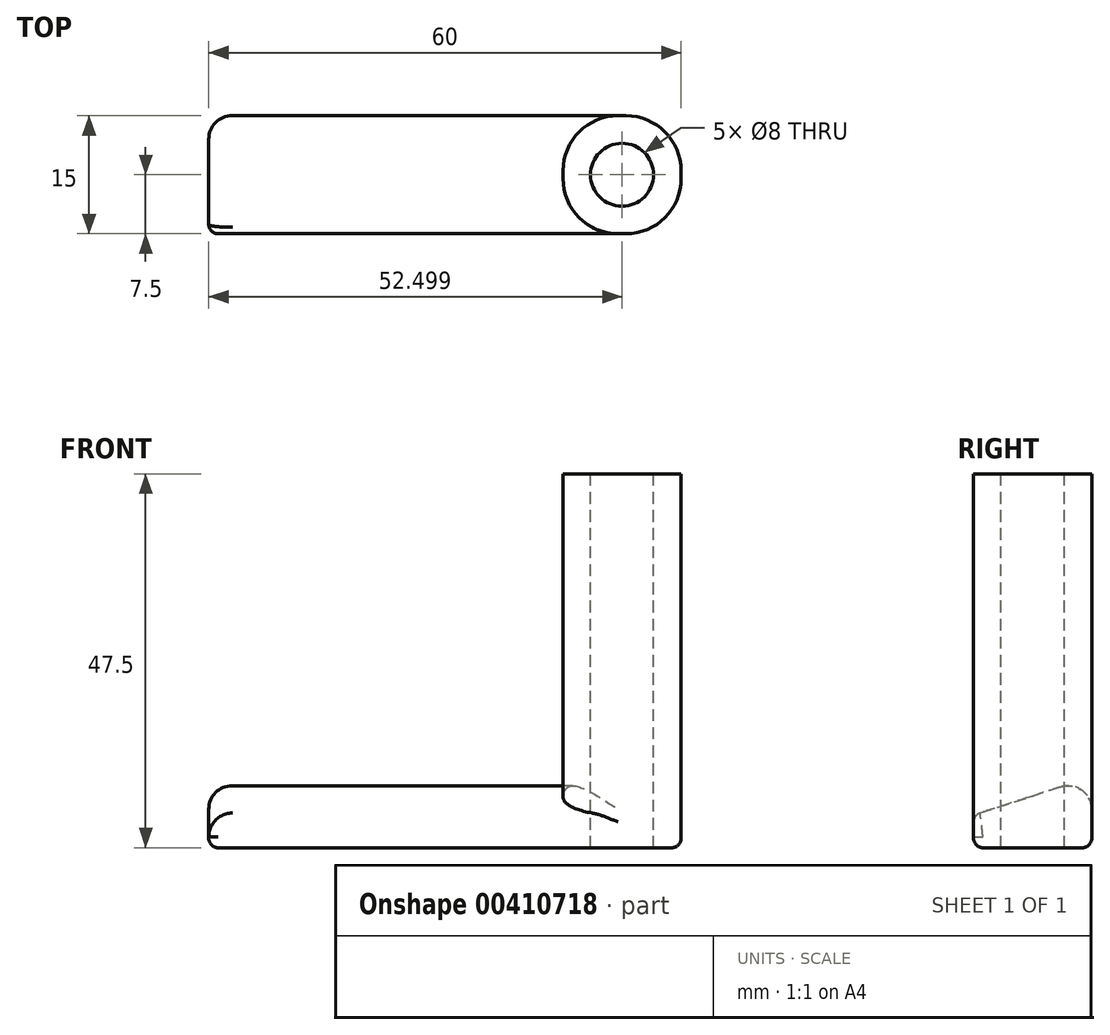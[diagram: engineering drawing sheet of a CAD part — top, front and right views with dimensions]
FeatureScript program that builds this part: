
annotation { "Feature Type Name" : "Feature", "Feature Type Description" : "" }
export const myFeature = defineFeature(function(context is Context, id is Id, definition is map)
    precondition{}
    {
        {
            var Q0;
            Q0=qCreatedBy(makeId("Front.planeOp"),FACE);
            var sketch = newSketch(context, id + "F0", { "sketchPlane" : qUnion([Q0])});
            skLineSegment(sketch, "E0", {"start": v(-36.94, 0) * mm, "end": v(23.06, 0) * mm});
            skLineSegment(sketch, "E1", {"start": v(23.06, 0) * mm, "end": v(23.06, 47.5) * mm});
            skLineSegment(sketch, "E2", {"start": v(23.06, 47.5) * mm, "end": v(8.06, 47.5) * mm});
            skLineSegment(sketch, "E3", {"start": v(-36.94, 9.15) * mm, "end": v(-36.94, 0) * mm});
            skLineSegment(sketch, "E4", {"start": v(8.06, 47.5) * mm, "end": v(8.06, 9.15) * mm});
            skLineSegment(sketch, "E5", {"start": v(8.06, 9.15) * mm, "end": v(-36.94, 9.15) * mm});
            skSolve(sketch);
        }
        {
            var Q0;
            Q0=makeQuery(id+"F0.imprint","IMPRINT",FACE,{"disambiguationData":[TD([[makeQuery(id+"F0.imprint","IMPRINT",EDGE,{"derivedFrom":sQuery(id+"F0.wireOp",EDGE,"E0")}),1.0]])]});
            extrude(context, id + "F1", {"entities" : qUnion([Q0]), "depth" : 15 * mm});
        }
        {
            var Q0;
            Q0=makeQuery(id+"F1.opExtrude","SWEPT_FACE",FACE,{"disambiguationData":[OSD([sQuery(id+"F0.wireOp",EDGE,"E2")])]});
            var sketch = newSketch(context, id + "F2", { "sketchPlane" : qUnion([Q0])});
            skCircle(sketch, "E6", {"center": v(15.56, -7.5) * mm, "radius": 4 * mm});
            skPoint(sketch, "E6.centerSnap0", {"position": v(15.56, 0) * mm});
            skPoint(sketch, "E6.centerSnap1", {"position": v(23.06, -7.5) * mm});
            skSolve(sketch);
        }
        {
            var Q0;
            Q0=makeQuery(id+"F2.imprint","IMPRINT",FACE,{"disambiguationData":[TD([[makeQuery(id+"F2.imprint","IMPRINT",EDGE,{"derivedFrom":sQuery(id+"F2.wireOp",EDGE,"E6")}),1.0]])]});
            extrude(context, id + "F3", {"entities" : qUnion([Q0]), "operationType" : NewBodyOperationType.REMOVE, "oppositeDirection" : true, "depth" : 55.9 * mm});
        }
        {
            var Q0;
            Q0=makeQuery(id+"F1.opExtrude","CAP_EDGE",EDGE,{"disambiguationData":[OSD([sQuery(id+"F0.wireOp",EDGE,"E5")])],"isStart":false});
            chamfer(context, id + "F4", {"entities" : qUnion([Q0]), "chamferType" : ChamferType.OFFSET_ANGLE, "width" : 5 * mm, "oppositeDirection" : false, "angle" : 72 * degree, "tangentPropagation" : true});
        }
        {
            var Q0;
            Q0=makeQuery(id+"F1.opExtrude","CAP_EDGE",EDGE,{"disambiguationData":[OSD([sQuery(id+"F0.wireOp",EDGE,"E4")])],"isStart":false});
            var Q1;
            Q1=makeQuery(id+"F1.opExtrude","CAP_EDGE",EDGE,{"disambiguationData":[OSD([sQuery(id+"F0.wireOp",EDGE,"E4")])],"isStart":true});
            var Q2;
            Q2=makeQuery(id+"F1.opExtrude","CAP_EDGE",EDGE,{"disambiguationData":[OSD([sQuery(id+"F0.wireOp",EDGE,"E1")])],"isStart":true});
            var Q3;
            Q3=makeQuery(id+"F1.opExtrude","CAP_EDGE",EDGE,{"disambiguationData":[OSD([sQuery(id+"F0.wireOp",EDGE,"E1")])],"isStart":false});
            fillet(context, id + "F5", {"entities" : qUnion([Q0, Q1, Q2, Q3]), "radius" : 7 * mm, "tangentPropagation" : true, "allowEdgeOverflow" : false});
        }
        {
            var Q0;
            {var subQ0=sQuery(id+"F0.wireOp",EDGE,"E5");Q0=makeQuery(id+"F4.opChamfer","BLEND_EDGE",EDGE,{"blendedFrom":[makeQuery(id+"F1.opExtrude","CAP_EDGE",EDGE,{"disambiguationData":[OSD([subQ0])],"isStart":false}),makeQuery(id+"F1.opExtrude","CAP_FACE",FACE,{"disambiguationData":[OSD([sQuery(id+"F0.wireOp",EDGE,"E0"),sQuery(id+"F0.wireOp",EDGE,"E1"),sQuery(id+"F0.wireOp",EDGE,"E2"),sQuery(id+"F0.wireOp",EDGE,"E3"),sQuery(id+"F0.wireOp",EDGE,"E4"),subQ0])],"isStart":true})],"blendedInto":[makeQuery(id+"F1.opExtrude","CAP_FACE",FACE,{"disambiguationData":[OSD([sQuery(id+"F0.wireOp",EDGE,"E0"),sQuery(id+"F0.wireOp",EDGE,"E1"),sQuery(id+"F0.wireOp",EDGE,"E2"),sQuery(id+"F0.wireOp",EDGE,"E3"),sQuery(id+"F0.wireOp",EDGE,"E4"),subQ0])],"isStart":true})]});}
            fillet(context, id + "F6", {"entities" : qUnion([Q0]), "radius" : 3 * mm, "tangentPropagation" : true, "allowEdgeOverflow" : false});
        }
        {
            var Q0;
            Q0=makeQuery(id+"F1.opExtrude","CAP_EDGE",EDGE,{"disambiguationData":[OSD([sQuery(id+"F0.wireOp",EDGE,"E3")])],"isStart":true});
            fillet(context, id + "F7", {"entities" : qUnion([Q0]), "radius" : 3 * mm, "tangentPropagation" : true, "allowEdgeOverflow" : false});
        }
        {
            var Q0;
            Q0=makeQuery(id+"F1.opExtrude","CAP_EDGE",EDGE,{"disambiguationData":[OSD([sQuery(id+"F0.wireOp",EDGE,"E0")])],"isStart":true});
            var Q1;
            Q1=makeQuery(id+"F1.opExtrude","CAP_EDGE",EDGE,{"disambiguationData":[OSD([sQuery(id+"F0.wireOp",EDGE,"E0")])],"isStart":false});
            var Q2;
            Q2=makeQuery(id+"F5.opFillet","BLEND_EDGE",EDGE,{"blendedFrom":[makeQuery(id+"F1.opExtrude","CAP_EDGE",EDGE,{"disambiguationData":[OSD([sQuery(id+"F0.wireOp",EDGE,"E1")])],"isStart":true}),makeQuery(id+"F1.opExtrude","SWEPT_FACE",FACE,{"disambiguationData":[OSD([sQuery(id+"F0.wireOp",EDGE,"E0")])]})],"blendedInto":[makeQuery(id+"F1.opExtrude","SWEPT_FACE",FACE,{"disambiguationData":[OSD([sQuery(id+"F0.wireOp",EDGE,"E0")])]})]});
            var Q3;
            Q3=makeQuery(id+"F5.opFillet","BLEND_EDGE",EDGE,{"blendedFrom":[makeQuery(id+"F1.opExtrude","CAP_EDGE",EDGE,{"disambiguationData":[OSD([sQuery(id+"F0.wireOp",EDGE,"E1")])],"isStart":false}),makeQuery(id+"F1.opExtrude","SWEPT_FACE",FACE,{"disambiguationData":[OSD([sQuery(id+"F0.wireOp",EDGE,"E0")])]})],"blendedInto":[makeQuery(id+"F1.opExtrude","SWEPT_FACE",FACE,{"disambiguationData":[OSD([sQuery(id+"F0.wireOp",EDGE,"E0")])]})]});
            var Q4;
            Q4=makeQuery(id+"F1.opExtrude","SWEPT_EDGE",EDGE,{"disambiguationData":[OSD([sQuery(id+"F0.wireOp",EDGE,"E0"),sQuery(id+"F0.wireOp",EDGE,"E1")])]});
            var Q5;
            Q5=makeQuery(id+"F7.opFillet","BLEND_EDGE",EDGE,{"blendedFrom":[makeQuery(id+"F1.opExtrude","CAP_EDGE",EDGE,{"disambiguationData":[OSD([sQuery(id+"F0.wireOp",EDGE,"E3")])],"isStart":true}),makeQuery(id+"F1.opExtrude","SWEPT_FACE",FACE,{"disambiguationData":[OSD([sQuery(id+"F0.wireOp",EDGE,"E0")])]})],"blendedInto":[makeQuery(id+"F1.opExtrude","SWEPT_FACE",FACE,{"disambiguationData":[OSD([sQuery(id+"F0.wireOp",EDGE,"E0")])]})]});
            var Q6;
            Q6=makeQuery(id+"F1.opExtrude","SWEPT_EDGE",EDGE,{"disambiguationData":[OSD([sQuery(id+"F0.wireOp",EDGE,"E0"),sQuery(id+"F0.wireOp",EDGE,"E3")])]});
            var Q7;
            {var subQ0=sQuery(id+"F0.wireOp",EDGE,"E5");Q7=makeQuery(id+"F4.opChamfer","BLEND_EDGE",EDGE,{"blendedFrom":[makeQuery(id+"F1.opExtrude","CAP_EDGE",EDGE,{"disambiguationData":[OSD([subQ0])],"isStart":false}),makeQuery(id+"F1.opExtrude","CAP_FACE",FACE,{"disambiguationData":[OSD([sQuery(id+"F0.wireOp",EDGE,"E0"),sQuery(id+"F0.wireOp",EDGE,"E1"),sQuery(id+"F0.wireOp",EDGE,"E2"),sQuery(id+"F0.wireOp",EDGE,"E3"),sQuery(id+"F0.wireOp",EDGE,"E4"),subQ0])],"isStart":false})],"blendedInto":[makeQuery(id+"F1.opExtrude","CAP_FACE",FACE,{"disambiguationData":[OSD([sQuery(id+"F0.wireOp",EDGE,"E0"),sQuery(id+"F0.wireOp",EDGE,"E1"),sQuery(id+"F0.wireOp",EDGE,"E2"),sQuery(id+"F0.wireOp",EDGE,"E3"),sQuery(id+"F0.wireOp",EDGE,"E4"),subQ0])],"isStart":false})]});}
            fillet(context, id + "F8", {"entities" : qUnion([Q0, Q1, Q2, Q3, Q4, Q5, Q6, Q7]), "radius" : 1.2 * mm, "tangentPropagation" : true, "allowEdgeOverflow" : false});
        }
    });
